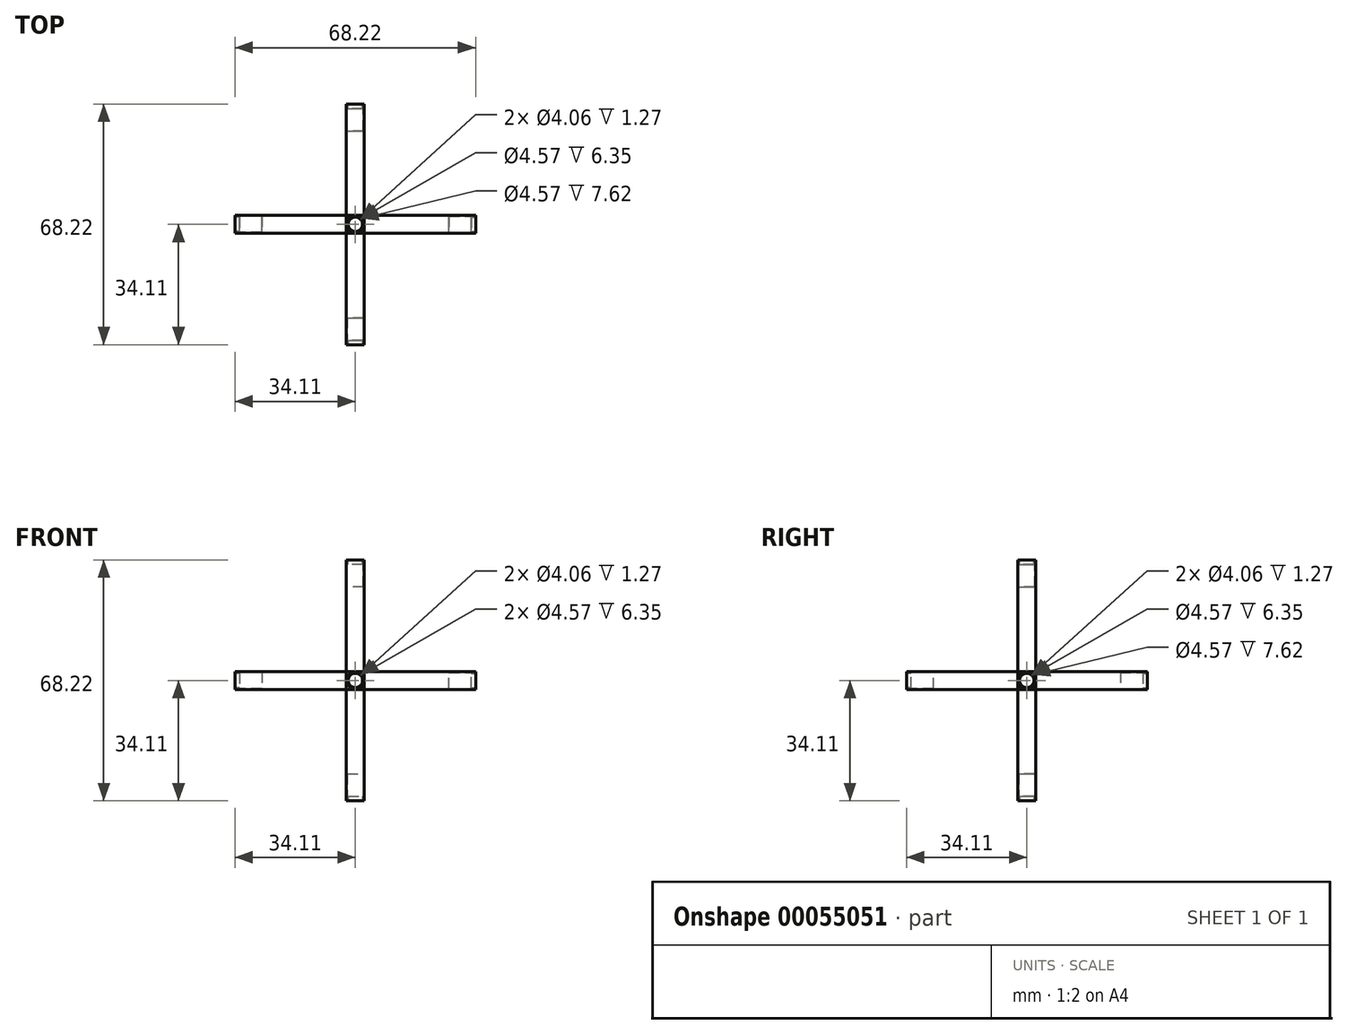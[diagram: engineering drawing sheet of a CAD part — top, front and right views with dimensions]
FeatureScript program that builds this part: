
annotation { "Feature Type Name" : "Feature", "Feature Type Description" : "" }
export const myFeature = defineFeature(function(context is Context, id is Id, definition is map)
    precondition{}
    {
        {
            var Q0;
            Q0=qCreatedBy(makeId("Top.planeOp"),FACE);
            var sketch = newSketch(context, id + "F0", { "sketchPlane" : qUnion([Q0])});
            skLineSegment(sketch, "E0.bottom", {"start": v(-2.54, 2.54) * mm, "end": v(2.54, 2.54) * mm});
            skLineSegment(sketch, "E0.top", {"start": v(-2.54, -2.54) * mm, "end": v(2.54, -2.54) * mm});
            skLineSegment(sketch, "E0.left", {"start": v(-2.54, 2.54) * mm, "end": v(-2.54, -2.54) * mm});
            skLineSegment(sketch, "E0.right", {"start": v(2.54, 2.54) * mm, "end": v(2.54, -2.54) * mm});
            skLineSegment(sketch, "E1", {"start": v(0, 2.54) * mm, "end": v(0, -2.54) * mm});
            skLineSegment(sketch, "E2", {"start": v(0, -2.54) * mm, "end": v(2.54, 0) * mm});
            skLineSegment(sketch, "E3", {"start": v(2.54, 0) * mm, "end": v(-2.54, 0) * mm});
            skPoint(sketch, "E4", {"position": v(0, 0) * mm});
            skLineSegment(sketch, "E5", {"start": v(-2.54, 0) * mm, "end": v(-2.54, 2.54) * mm});
            skLineSegment(sketch, "E6", {"start": v(0, 2.54) * mm, "end": v(-2.54, 2.54) * mm});
            skSolve(sketch);
        }
        {
            var Q0;
            {var subQ4=sQuery(id+"F0.wireOp",EDGE,"E5");Q0=makeQuery(id+"F0.imprint","IMPRINT",FACE,{"disambiguationData":[TD([[makeQuery(id+"F0.imprint","IMPRINT",EDGE,{"derivedFrom":subQ4}),-1.0]])]});}
            var Q1;
            {var subQ0=sQuery(id+"F0.wireOp",EDGE,"E0.bottom");Q1=makeQuery(id+"F0.imprint","IMPRINT",FACE,{"disambiguationData":[TD([[makeQuery(id+"F0.imprint","IMPRINT",EDGE,{"derivedFrom":subQ0}),-1.0]])]});}
            var Q2;
            {var subQ3=sQuery(id+"F0.wireOp",EDGE,"E2");Q2=makeQuery(id+"F0.imprint","IMPRINT",FACE,{"disambiguationData":[TD([[makeQuery(id+"F0.imprint","IMPRINT",EDGE,{"derivedFrom":subQ3}),-1.0]])]});}
            var Q3;
            {var subQ0=sQuery(id+"F0.wireOp",EDGE,"E2");Q3=makeQuery(id+"F0.imprint","IMPRINT",FACE,{"disambiguationData":[TD([[makeQuery(id+"F0.imprint","IMPRINT",EDGE,{"derivedFrom":subQ0}),1.0]])]});}
            var Q4;
            {var subQ0=sQuery(id+"F0.wireOp",EDGE,"E0.left");Q4=makeQuery(id+"F0.imprint","IMPRINT",FACE,{"disambiguationData":[TD([[makeQuery(id+"F0.imprint","IMPRINT",EDGE,{"derivedFrom":subQ0}),1.0]])]});}
            extrude(context, id + "F1", {"entities" : qUnion([Q0, Q1, Q2, Q3, Q4]), "depth" : 5.08 * mm});
        }
        {
            var Q0;
            Q0=makeQuery(id+"F1.opExtrude","CAP_FACE",FACE,{"disambiguationData":[OSD([sQuery(id+"F0.wireOp",EDGE,"E0.bottom"),sQuery(id+"F0.wireOp",EDGE,"E0.top"),sQuery(id+"F0.wireOp",EDGE,"E0.left"),sQuery(id+"F0.wireOp",EDGE,"E0.right"),sQuery(id+"F0.wireOp",EDGE,"E5"),sQuery(id+"F0.wireOp",EDGE,"E6")])],"isStart":false});
            var sketch = newSketch(context, id + "F2", { "sketchPlane" : qUnion([Q0])});
            skPoint(sketch, "E7", {"position": v(0, 0) * mm});
            skCircle(sketch, "E8", {"center": v(0, 0) * mm, "radius": 2.54 * mm});
            skSolve(sketch);
        }
        {
            var Q0;
            Q0=makeQuery(id+"F1.opExtrude","SWEPT_FACE",FACE,{"disambiguationData":[OSD([sQuery(id+"F0.wireOp",EDGE,"E0.top")])]});
            var sketch = newSketch(context, id + "F3", { "sketchPlane" : qUnion([Q0])});
            skLineSegment(sketch, "E9", {"start": v(0, 5.08) * mm, "end": v(0, 0) * mm});
            skLineSegment(sketch, "E10", {"start": v(0, 0) * mm, "end": v(-2.54, 2.54) * mm});
            skLineSegment(sketch, "E11", {"start": v(-2.54, 2.54) * mm, "end": v(2.54, 2.54) * mm});
            skPoint(sketch, "E12", {"position": v(0, 2.54) * mm});
            skCircle(sketch, "E13", {"center": v(0, 2.54) * mm, "radius": 2.54 * mm});
            skSolve(sketch);
        }
        {
            var Q0;
            Q0=makeQuery(id+"F1.opExtrude","SWEPT_FACE",FACE,{"disambiguationData":[OSD([sQuery(id+"F0.wireOp",EDGE,"E0.bottom"),sQuery(id+"F0.wireOp",EDGE,"E6")])]});
            var sketch = newSketch(context, id + "F4", { "sketchPlane" : qUnion([Q0])});
            skPoint(sketch, "E14", {"position": v(0, 2.54) * mm});
            skCircle(sketch, "E15", {"center": v(0, 2.54) * mm, "radius": 2.54 * mm});
            skSolve(sketch);
        }
        {
            var Q0;
            Q0=makeQuery(id+"F1.opExtrude","SWEPT_FACE",FACE,{"disambiguationData":[OSD([sQuery(id+"F0.wireOp",EDGE,"E0.left"),sQuery(id+"F0.wireOp",EDGE,"E5")])]});
            var sketch = newSketch(context, id + "F5", { "sketchPlane" : qUnion([Q0])});
            skLineSegment(sketch, "E16", {"start": v(-2.54, 2.54) * mm, "end": v(2.54, 2.54) * mm});
            skLineSegment(sketch, "E17", {"start": v(2.54, 2.54) * mm, "end": v(0, 5.08) * mm});
            skLineSegment(sketch, "E18", {"start": v(0, 5.08) * mm, "end": v(0, 0) * mm});
            skCircle(sketch, "E19", {"center": v(0, 2.54) * mm, "radius": 2.54 * mm});
            skSolve(sketch);
        }
        {
            var Q0;
            Q0=makeQuery(id+"F1.opExtrude","SWEPT_FACE",FACE,{"disambiguationData":[OSD([sQuery(id+"F0.wireOp",EDGE,"E0.right")])]});
            var sketch = newSketch(context, id + "F6", { "sketchPlane" : qUnion([Q0])});
            skPoint(sketch, "E20", {"position": v(0, 2.54) * mm});
            skCircle(sketch, "E21", {"center": v(0, 2.54) * mm, "radius": 2.54 * mm});
            skSolve(sketch);
        }
        {
            var Q0;
            Q0=makeQuery(id+"F1.opExtrude","CAP_FACE",FACE,{"disambiguationData":[OSD([sQuery(id+"F0.wireOp",EDGE,"E0.bottom"),sQuery(id+"F0.wireOp",EDGE,"E0.top"),sQuery(id+"F0.wireOp",EDGE,"E0.left"),sQuery(id+"F0.wireOp",EDGE,"E0.right"),sQuery(id+"F0.wireOp",EDGE,"E5"),sQuery(id+"F0.wireOp",EDGE,"E6")])],"isStart":true});
            var sketch = newSketch(context, id + "F7", { "sketchPlane" : qUnion([Q0])});
            skCircle(sketch, "E22", {"center": v(0, 0) * mm, "radius": 2.54 * mm});
            skSolve(sketch);
        }
        {
            var Q0;
            {var subQ0=sQuery(id+"F7.wireOp",EDGE,"E22");var subQ1=makeQuery(id+"F7.imprint","INTERSECT",VERTEX,{"derivedFrom":[makeQuery(id+"F1.opExtrude","CAP_EDGE",EDGE,{"disambiguationData":[OSD([sQuery(id+"F0.wireOp",EDGE,"E0.top")])],"isStart":true}),subQ0]});Q0=makeQuery(id+"F7.imprint","IMPRINT",FACE,{"disambiguationData":[TD([[makeQuery(id+"F7.imprint","IMPRINT",EDGE,{"disambiguationData":[TD([[subQ1,1.0]])],"derivedFrom":subQ0}),1.0]])]});}
            extrude(context, id + "F8", {"entities" : qUnion([Q0]), "operationType" : NewBodyOperationType.ADD, "depth" : 31.57 * mm});
        }
        {
            var Q0;
            Q0=makeQuery(id+"F8.opExtrude","CAP_FACE",FACE,{"disambiguationData":[OSD([sQuery(id+"F7.wireOp",EDGE,"E22")])],"isStart":false});
            var sketch = newSketch(context, id + "F9", { "sketchPlane" : qUnion([Q0])});
            skPoint(sketch, "E23", {"position": v(0, 0) * mm});
            skCircle(sketch, "E24", {"center": v(0, 0) * mm, "radius": 2.29 * mm});
            skCircle(sketch, "E25", {"center": v(0, 0) * mm, "radius": 2.03 * mm});
            skSolve(sketch);
        }
        {
            var Q0;
            Q0=makeQuery(id+"F9.imprint","IMPRINT",FACE,{"disambiguationData":[TD([[makeQuery(id+"F9.imprint","IMPRINT",EDGE,{"derivedFrom":sQuery(id+"F9.wireOp",EDGE,"E24")}),1.0]])]});
            var Q1;
            Q1=makeQuery(id+"F9.imprint","IMPRINT",FACE,{"disambiguationData":[TD([[makeQuery(id+"F9.imprint","IMPRINT",EDGE,{"derivedFrom":sQuery(id+"F9.wireOp",EDGE,"E25")}),1.0]])]});
            extrude(context, id + "F10", {"entities" : qUnion([Q0, Q1]), "operationType" : NewBodyOperationType.REMOVE, "oppositeDirection" : true, "depth" : 7.62 * mm});
        }
        {
            var Q0;
            Q0=makeQuery(id+"F9.imprint","IMPRINT",FACE,{"disambiguationData":[TD([[makeQuery(id+"F9.imprint","IMPRINT",EDGE,{"derivedFrom":sQuery(id+"F9.wireOp",EDGE,"E24")}),1.0]])]});
            extrude(context, id + "F11", {"entities" : qUnion([Q0]), "operationType" : NewBodyOperationType.ADD, "oppositeDirection" : true, "depth" : 1.27 * mm});
        }
        {
            var Q0;
            {var subQ0=sQuery(id+"F6.wireOp",EDGE,"E21");var subQ1=sQuery(id+"F0.wireOp",EDGE,"E0.right");var subQ2=makeQuery(id+"F6.imprint","INTERSECT",VERTEX,{"derivedFrom":[makeQuery(id+"F1.opExtrude","CAP_EDGE",EDGE,{"disambiguationData":[OSD([subQ1])],"isStart":false}),subQ0]});Q0=makeQuery(id+"F6.imprint","IMPRINT",FACE,{"disambiguationData":[TD([[makeQuery(id+"F6.imprint","IMPRINT",EDGE,{"disambiguationData":[TD([[subQ2,1.0]])],"derivedFrom":subQ0}),1.0]])]});}
            extrude(context, id + "F12", {"entities" : qUnion([Q0]), "operationType" : NewBodyOperationType.ADD, "depth" : 31.57 * mm});
        }
        {
            var Q0;
            Q0=makeQuery(id+"F12.opExtrude","CAP_FACE",FACE,{"disambiguationData":[OSD([sQuery(id+"F6.wireOp",EDGE,"E21")])],"isStart":false});
            var sketch = newSketch(context, id + "F13", { "sketchPlane" : qUnion([Q0])});
            skPoint(sketch, "E26", {"position": v(0, 2.54) * mm});
            skCircle(sketch, "E27", {"center": v(0, 2.54) * mm, "radius": 2.29 * mm});
            skCircle(sketch, "E28", {"center": v(0, 2.54) * mm, "radius": 2.03 * mm});
            skSolve(sketch);
        }
        {
            var Q0;
            Q0=makeQuery(id+"F13.imprint","IMPRINT",FACE,{"disambiguationData":[TD([[makeQuery(id+"F13.imprint","IMPRINT",EDGE,{"derivedFrom":sQuery(id+"F13.wireOp",EDGE,"E27")}),1.0]])]});
            var Q1;
            Q1=makeQuery(id+"F13.imprint","IMPRINT",FACE,{"disambiguationData":[TD([[makeQuery(id+"F13.imprint","IMPRINT",EDGE,{"derivedFrom":sQuery(id+"F13.wireOp",EDGE,"E28")}),1.0]])]});
            extrude(context, id + "F14", {"entities" : qUnion([Q0, Q1]), "operationType" : NewBodyOperationType.REMOVE, "oppositeDirection" : true, "depth" : 7.62 * mm});
        }
        {
            var Q0;
            Q0=makeQuery(id+"F13.imprint","IMPRINT",FACE,{"disambiguationData":[TD([[makeQuery(id+"F13.imprint","IMPRINT",EDGE,{"derivedFrom":sQuery(id+"F13.wireOp",EDGE,"E27")}),1.0]])]});
            extrude(context, id + "F15", {"entities" : qUnion([Q0]), "operationType" : NewBodyOperationType.ADD, "oppositeDirection" : true, "depth" : 1.27 * mm});
        }
        {
            var Q0;
            {var subQ1=sQuery(id+"F3.wireOp",EDGE,"E9");var subQ4=sQuery(id+"F3.wireOp",EDGE,"E11");var subQ5=makeQuery(id+"F3.imprint","INTERSECT",VERTEX,{"derivedFrom":[subQ1,subQ4]});Q0=makeQuery(id+"F3.imprint","IMPRINT",FACE,{"disambiguationData":[TD([[makeQuery(id+"F3.imprint","IMPRINT",EDGE,{"disambiguationData":[TD([[subQ5,1.0]])],"derivedFrom":subQ1}),-1.0]])]});}
            var Q1;
            {var subQ1=sQuery(id+"F3.wireOp",EDGE,"E9");var subQ4=sQuery(id+"F3.wireOp",EDGE,"E11");var subQ5=makeQuery(id+"F3.imprint","INTERSECT",VERTEX,{"derivedFrom":[subQ1,subQ4]});Q1=makeQuery(id+"F3.imprint","IMPRINT",FACE,{"disambiguationData":[TD([[makeQuery(id+"F3.imprint","IMPRINT",EDGE,{"disambiguationData":[TD([[subQ5,1.0]])],"derivedFrom":subQ1}),1.0]])]});}
            var Q2;
            {var subQ1=sQuery(id+"F3.wireOp",EDGE,"E9");var subQ4=sQuery(id+"F3.wireOp",EDGE,"E11");var subQ5=makeQuery(id+"F3.imprint","INTERSECT",VERTEX,{"derivedFrom":[subQ1,subQ4]});Q2=makeQuery(id+"F3.imprint","IMPRINT",FACE,{"disambiguationData":[TD([[makeQuery(id+"F3.imprint","IMPRINT",EDGE,{"disambiguationData":[TD([[subQ5,-1.0]])],"derivedFrom":subQ1}),1.0]])]});}
            var Q3;
            {var subQ1=sQuery(id+"F3.wireOp",EDGE,"E10");Q3=makeQuery(id+"F3.imprint","IMPRINT",FACE,{"disambiguationData":[TD([[makeQuery(id+"F3.imprint","IMPRINT",EDGE,{"derivedFrom":subQ1}),-1.0]])]});}
            var Q4;
            {var subQ0=sQuery(id+"F3.wireOp",EDGE,"E10");Q4=makeQuery(id+"F3.imprint","IMPRINT",FACE,{"disambiguationData":[TD([[makeQuery(id+"F3.imprint","IMPRINT",EDGE,{"derivedFrom":subQ0}),1.0]])]});}
            extrude(context, id + "F16", {"entities" : qUnion([Q0, Q1, Q2, Q3, Q4]), "operationType" : NewBodyOperationType.ADD, "depth" : 31.57 * mm});
        }
        {
            var Q0;
            Q0=makeQuery(id+"F16.opExtrude","CAP_FACE",FACE,{"disambiguationData":[OSD([sQuery(id+"F3.wireOp",EDGE,"E13")])],"isStart":false});
            var sketch = newSketch(context, id + "F17", { "sketchPlane" : qUnion([Q0])});
            skPoint(sketch, "E29", {"position": v(0, 2.54) * mm});
            skCircle(sketch, "E30", {"center": v(0, 2.54) * mm, "radius": 2.29 * mm});
            skCircle(sketch, "E31", {"center": v(0, 2.54) * mm, "radius": 2.03 * mm});
            skSolve(sketch);
        }
        {
            var Q0;
            Q0=makeQuery(id+"F17.imprint","IMPRINT",FACE,{"disambiguationData":[TD([[makeQuery(id+"F17.imprint","IMPRINT",EDGE,{"derivedFrom":sQuery(id+"F17.wireOp",EDGE,"E30")}),1.0]])]});
            var Q1;
            Q1=makeQuery(id+"F17.imprint","IMPRINT",FACE,{"disambiguationData":[TD([[makeQuery(id+"F17.imprint","IMPRINT",EDGE,{"derivedFrom":sQuery(id+"F17.wireOp",EDGE,"E31")}),1.0]])]});
            extrude(context, id + "F18", {"entities" : qUnion([Q0, Q1]), "operationType" : NewBodyOperationType.REMOVE, "oppositeDirection" : true, "depth" : 7.62 * mm});
        }
        {
            var Q0;
            Q0=makeQuery(id+"F17.imprint","IMPRINT",FACE,{"disambiguationData":[TD([[makeQuery(id+"F17.imprint","IMPRINT",EDGE,{"derivedFrom":sQuery(id+"F17.wireOp",EDGE,"E30")}),1.0]])]});
            extrude(context, id + "F19", {"entities" : qUnion([Q0]), "operationType" : NewBodyOperationType.ADD, "oppositeDirection" : true, "depth" : 1.27 * mm});
        }
        {
            var Q0;
            {var subQ0=sQuery(id+"F4.wireOp",EDGE,"E15");var subQ1=sQuery(id+"F0.wireOp",EDGE,"E6");var subQ2=sQuery(id+"F0.wireOp",EDGE,"E0.bottom");var subQ3=makeQuery(id+"F4.imprint","INTERSECT",VERTEX,{"derivedFrom":[makeQuery(id+"F1.opExtrude","CAP_EDGE",EDGE,{"disambiguationData":[OSD([subQ2,subQ1])],"isStart":false}),subQ0]});Q0=makeQuery(id+"F4.imprint","IMPRINT",FACE,{"disambiguationData":[TD([[makeQuery(id+"F4.imprint","IMPRINT",EDGE,{"disambiguationData":[TD([[subQ3,1.0]])],"derivedFrom":subQ0}),1.0]])]});}
            extrude(context, id + "F20", {"entities" : qUnion([Q0]), "operationType" : NewBodyOperationType.ADD, "depth" : 31.57 * mm});
        }
        {
            var Q0;
            Q0=makeQuery(id+"F20.opExtrude","CAP_FACE",FACE,{"disambiguationData":[OSD([sQuery(id+"F4.wireOp",EDGE,"E15")])],"isStart":false});
            var sketch = newSketch(context, id + "F21", { "sketchPlane" : qUnion([Q0])});
            skPoint(sketch, "E32", {"position": v(0, 2.54) * mm});
            skCircle(sketch, "E33", {"center": v(0, 2.54) * mm, "radius": 2.03 * mm});
            skCircle(sketch, "E34", {"center": v(0, 2.54) * mm, "radius": 2.29 * mm});
            skSolve(sketch);
        }
        {
            var Q0;
            Q0=makeQuery(id+"F21.imprint","IMPRINT",FACE,{"disambiguationData":[TD([[makeQuery(id+"F21.imprint","IMPRINT",EDGE,{"derivedFrom":sQuery(id+"F21.wireOp",EDGE,"E33")}),-1.0]])]});
            var Q1;
            Q1=makeQuery(id+"F21.imprint","IMPRINT",FACE,{"disambiguationData":[TD([[makeQuery(id+"F21.imprint","IMPRINT",EDGE,{"derivedFrom":sQuery(id+"F21.wireOp",EDGE,"E33")}),1.0]])]});
            extrude(context, id + "F22", {"entities" : qUnion([Q0, Q1]), "operationType" : NewBodyOperationType.REMOVE, "oppositeDirection" : true, "depth" : 7.62 * mm});
        }
        {
            var Q0;
            Q0=makeQuery(id+"F21.imprint","IMPRINT",FACE,{"disambiguationData":[TD([[makeQuery(id+"F21.imprint","IMPRINT",EDGE,{"derivedFrom":sQuery(id+"F21.wireOp",EDGE,"E33")}),-1.0]])]});
            extrude(context, id + "F23", {"entities" : qUnion([Q0]), "operationType" : NewBodyOperationType.ADD, "oppositeDirection" : true, "depth" : 1.27 * mm});
        }
        {
            var Q0;
            {var subQ0=sQuery(id+"F2.wireOp",EDGE,"E8");var subQ2=makeQuery(id+"F2.imprint","INTERSECT",VERTEX,{"derivedFrom":[makeQuery(id+"F1.opExtrude","CAP_EDGE",EDGE,{"disambiguationData":[OSD([sQuery(id+"F0.wireOp",EDGE,"E0.right")])],"isStart":false}),subQ0]});Q0=makeQuery(id+"F2.imprint","IMPRINT",FACE,{"disambiguationData":[TD([[makeQuery(id+"F2.imprint","IMPRINT",EDGE,{"disambiguationData":[TD([[subQ2,1.0]])],"derivedFrom":subQ0}),1.0]])]});}
            extrude(context, id + "F24", {"entities" : qUnion([Q0]), "operationType" : NewBodyOperationType.ADD, "depth" : 31.57 * mm});
        }
        {
            var Q0;
            Q0=makeQuery(id+"F24.opExtrude","CAP_FACE",FACE,{"disambiguationData":[OSD([sQuery(id+"F2.wireOp",EDGE,"E8")])],"isStart":false});
            var sketch = newSketch(context, id + "F25", { "sketchPlane" : qUnion([Q0])});
            skPoint(sketch, "E35", {"position": v(0, 0) * mm});
            skCircle(sketch, "E36", {"center": v(0, 0) * mm, "radius": 2.03 * mm});
            skCircle(sketch, "E37", {"center": v(0, 0) * mm, "radius": 2.29 * mm});
            skSolve(sketch);
        }
        {
            var Q0;
            Q0=makeQuery(id+"F25.imprint","IMPRINT",FACE,{"disambiguationData":[TD([[makeQuery(id+"F25.imprint","IMPRINT",EDGE,{"derivedFrom":sQuery(id+"F25.wireOp",EDGE,"E36")}),-1.0]])]});
            var Q1;
            Q1=makeQuery(id+"F25.imprint","IMPRINT",FACE,{"disambiguationData":[TD([[makeQuery(id+"F25.imprint","IMPRINT",EDGE,{"derivedFrom":sQuery(id+"F25.wireOp",EDGE,"E36")}),1.0]])]});
            extrude(context, id + "F26", {"entities" : qUnion([Q0, Q1]), "operationType" : NewBodyOperationType.REMOVE, "oppositeDirection" : true, "depth" : 7.62 * mm});
        }
        {
            var Q0;
            Q0=makeQuery(id+"F25.imprint","IMPRINT",FACE,{"disambiguationData":[TD([[makeQuery(id+"F25.imprint","IMPRINT",EDGE,{"derivedFrom":sQuery(id+"F25.wireOp",EDGE,"E36")}),-1.0]])]});
            extrude(context, id + "F27", {"entities" : qUnion([Q0]), "oppositeDirection" : true, "depth" : 1.27 * mm});
        }
        {
            var Q0;
            {var subQ1=sQuery(id+"F5.wireOp",EDGE,"E17");Q0=makeQuery(id+"F5.imprint","IMPRINT",FACE,{"disambiguationData":[TD([[makeQuery(id+"F5.imprint","IMPRINT",EDGE,{"derivedFrom":subQ1}),1.0]])]});}
            var Q1;
            {var subQ0=sQuery(id+"F5.wireOp",EDGE,"E17");Q1=makeQuery(id+"F5.imprint","IMPRINT",FACE,{"disambiguationData":[TD([[makeQuery(id+"F5.imprint","IMPRINT",EDGE,{"derivedFrom":subQ0}),-1.0]])]});}
            var Q2;
            {var subQ1=sQuery(id+"F5.wireOp",EDGE,"E16");var subQ4=sQuery(id+"F5.wireOp",EDGE,"E18");var subQ5=makeQuery(id+"F5.imprint","INTERSECT",VERTEX,{"derivedFrom":[subQ1,subQ4]});Q2=makeQuery(id+"F5.imprint","IMPRINT",FACE,{"disambiguationData":[TD([[makeQuery(id+"F5.imprint","IMPRINT",EDGE,{"disambiguationData":[TD([[subQ5,-1.0]])],"derivedFrom":subQ4}),1.0]])]});}
            var Q3;
            {var subQ1=sQuery(id+"F5.wireOp",EDGE,"E16");var subQ4=sQuery(id+"F5.wireOp",EDGE,"E18");var subQ5=makeQuery(id+"F5.imprint","INTERSECT",VERTEX,{"derivedFrom":[subQ1,subQ4]});Q3=makeQuery(id+"F5.imprint","IMPRINT",FACE,{"disambiguationData":[TD([[makeQuery(id+"F5.imprint","IMPRINT",EDGE,{"disambiguationData":[TD([[subQ5,1.0]])],"derivedFrom":subQ1}),1.0]])]});}
            var Q4;
            {var subQ1=sQuery(id+"F5.wireOp",EDGE,"E16");var subQ4=sQuery(id+"F5.wireOp",EDGE,"E18");var subQ5=makeQuery(id+"F5.imprint","INTERSECT",VERTEX,{"derivedFrom":[subQ1,subQ4]});Q4=makeQuery(id+"F5.imprint","IMPRINT",FACE,{"disambiguationData":[TD([[makeQuery(id+"F5.imprint","IMPRINT",EDGE,{"disambiguationData":[TD([[subQ5,1.0]])],"derivedFrom":subQ1}),-1.0]])]});}
            extrude(context, id + "F28", {"entities" : qUnion([Q0, Q1, Q2, Q3, Q4]), "operationType" : NewBodyOperationType.ADD, "depth" : 31.57 * mm});
        }
        {
            var Q0;
            Q0=makeQuery(id+"F28.opExtrude","CAP_FACE",FACE,{"disambiguationData":[OSD([sQuery(id+"F5.wireOp",EDGE,"E19")])],"isStart":false});
            var sketch = newSketch(context, id + "F29", { "sketchPlane" : qUnion([Q0])});
            skPoint(sketch, "E38", {"position": v(0, 2.54) * mm});
            skCircle(sketch, "E39", {"center": v(0, 2.54) * mm, "radius": 2.03 * mm});
            skCircle(sketch, "E40", {"center": v(0, 2.54) * mm, "radius": 2.29 * mm});
            skSolve(sketch);
        }
        {
            var Q0;
            Q0=makeQuery(id+"F29.imprint","IMPRINT",FACE,{"disambiguationData":[TD([[makeQuery(id+"F29.imprint","IMPRINT",EDGE,{"derivedFrom":sQuery(id+"F29.wireOp",EDGE,"E39")}),-1.0]])]});
            var Q1;
            Q1=makeQuery(id+"F29.imprint","IMPRINT",FACE,{"disambiguationData":[TD([[makeQuery(id+"F29.imprint","IMPRINT",EDGE,{"derivedFrom":sQuery(id+"F29.wireOp",EDGE,"E39")}),1.0]])]});
            extrude(context, id + "F30", {"entities" : qUnion([Q0, Q1]), "operationType" : NewBodyOperationType.REMOVE, "oppositeDirection" : true, "depth" : 7.62 * mm});
        }
        {
            var Q0;
            Q0=makeQuery(id+"F29.imprint","IMPRINT",FACE,{"disambiguationData":[TD([[makeQuery(id+"F29.imprint","IMPRINT",EDGE,{"derivedFrom":sQuery(id+"F29.wireOp",EDGE,"E39")}),-1.0]])]});
            extrude(context, id + "F31", {"entities" : qUnion([Q0]), "oppositeDirection" : true, "depth" : 1.27 * mm});
        }
    });
